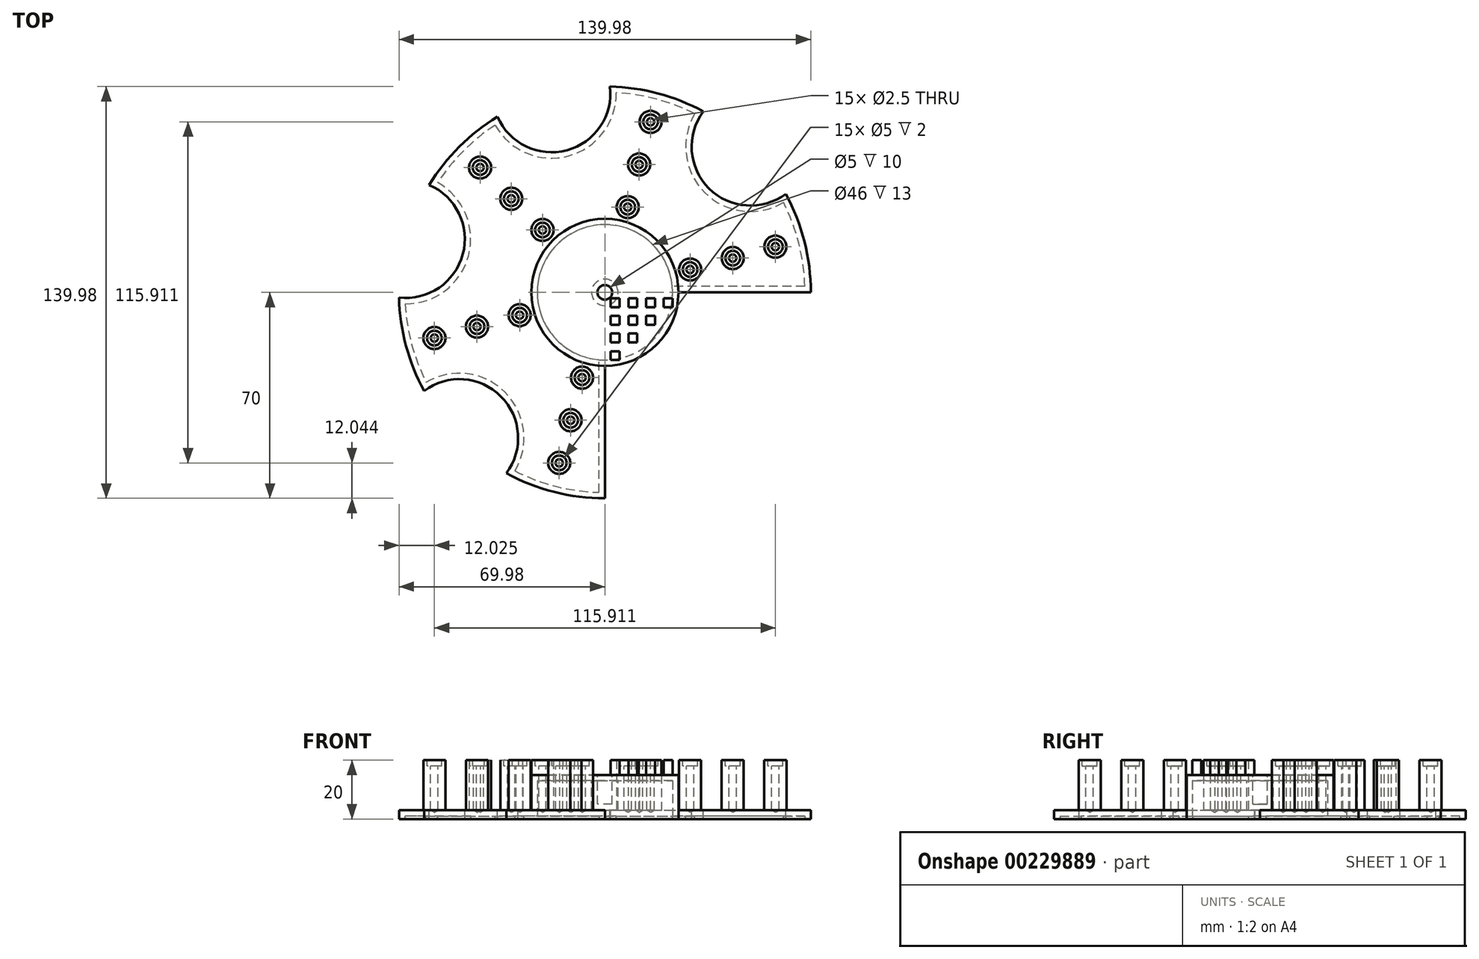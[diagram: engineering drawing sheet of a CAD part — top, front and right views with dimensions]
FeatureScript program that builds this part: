
annotation { "Feature Type Name" : "Feature", "Feature Type Description" : "" }
export const myFeature = defineFeature(function(context is Context, id is Id, definition is map)
    precondition{}
    {
        {
            var Q0;
            Q0=qCreatedBy(makeId("Top.planeOp"),FACE);
            var sketch = newSketch(context, id + "F0", { "sketchPlane" : qUnion([Q0])});
            skCircle(sketch, "E0", {"center": v(0, 0) * mm, "radius": 70 * mm});
            skSolve(sketch);
        }
        {
            var Q0;
            Q0 = qSketchRegion(id + "F0", true);
            extrude(context, id + "F1", {"entities" : qUnion([Q0]), "depth" : 10 * mm, "hasSecondDirection" : true, "secondDirectionOppositeDirection" : true, "secondDirectionDepth" : 5 * mm});
        }
        {
            var Q0;
            Q0=qCreatedBy(makeId("Front.planeOp"),FACE);
            var sketch = newSketch(context, id + "F2", { "sketchPlane" : qUnion([Q0])});
            skLineSegment(sketch, "E1", {"start": v(25, 20) * mm, "end": v(25, -2) * mm});
            skLineSegment(sketch, "E2", {"start": v(25, -2) * mm, "end": v(80, -2) * mm});
            skLineSegment(sketch, "E3", {"start": v(80, -2) * mm, "end": v(80, 20) * mm});
            skLineSegment(sketch, "E4", {"start": v(80, 20) * mm, "end": v(25, 20) * mm});
            skLineSegment(sketch, "E5", {"start": v(0, 50.21) * mm, "end": v(0, -31.63) * mm, "construction": true});
            skSolve(sketch);
        }
        {
            var Q0;
            Q0 = qSketchRegion(id + "F2", true);
            var Q1;
            Q1=sQuery(id+"F2.wireOp",EDGE,"E5");
            revolve(context, id + "F3", {"operationType" : NewBodyOperationType.REMOVE, "entities" : qUnion([Q0]), "axis" : qUnion([Q1]), "revolveType" : RevolveType.FULL, "oppositeDirection" : true});
        }
        {
            var Q0;
            Q0=makeQuery(id+"F1.opExtrude","CAP_FACE",FACE,{"disambiguationData":[OSD([sQuery(id+"F0.wireOp",EDGE,"E0")])],"isStart":false});
            var sketch = newSketch(context, id + "F4", { "sketchPlane" : qUnion([Q0])});
            skCircle(sketch, "E6", {"center": v(0, 0) * mm, "radius": 2.5 * mm});
            skSolve(sketch);
        }
        {
            var Q0;
            Q0 = qSketchRegion(id + "F4", true);
            extrude(context, id + "F5", {"entities" : qUnion([Q0]), "operationType" : NewBodyOperationType.REMOVE, "oppositeDirection" : true, "depth" : 10 * mm});
        }
        {
            var Q0;
            Q0=makeQuery(id+"F3.boolean.opBoolean","COPY",FACE,{"derivedFrom":makeQuery(id+"F3.opRevolve","SWEPT_FACE",FACE,{"disambiguationData":[OSD([sQuery(id+"F2.wireOp",EDGE,"E2")])]})});
            var sketch = newSketch(context, id + "F6", { "sketchPlane" : qUnion([Q0])});
            skLineSegment(sketch, "E7", {"start": v(0, 0) * mm, "end": v(-22.8, 85.11) * mm, "construction": true});
            skLineSegment(sketch, "E8", {"start": v(0, 0) * mm, "end": v(55.72, 55.72) * mm, "construction": true});
            skLineSegment(sketch, "E9", {"start": v(0, 0) * mm, "end": v(-80.55, 21.58) * mm, "construction": true});
            skLineSegment(sketch, "E10", {"start": v(0, 0) * mm, "end": v(-61.33, -61.33) * mm, "construction": true});
            skCircle(sketch, "E11", {"center": v(49.5, 49.5) * mm, "radius": 20 * mm});
            skCircle(sketch, "E12", {"center": v(-18.12, 67.61) * mm, "radius": 20 * mm});
            skCircle(sketch, "E13", {"center": v(-67.61, 18.12) * mm, "radius": 20 * mm});
            skCircle(sketch, "E14", {"center": v(-49.5, -49.5) * mm, "radius": 20 * mm});
            skSolve(sketch);
        }
        {
            var Q0;
            Q0 = qSketchRegion(id + "F6", true);
            extrude(context, id + "F7", {"entities" : qUnion([Q0]), "operationType" : NewBodyOperationType.REMOVE, "endBound" : BoundingType.THROUGH_ALL, "oppositeDirection" : true, "depth" : 25 * mm});
        }
        {
            var Q0;
            Q0=makeQuery(id+"F3.boolean.opBoolean","COPY",FACE,{"derivedFrom":makeQuery(id+"F3.opRevolve","SWEPT_FACE",FACE,{"disambiguationData":[OSD([sQuery(id+"F2.wireOp",EDGE,"E2")])]})});
            var sketch = newSketch(context, id + "F8", { "sketchPlane" : qUnion([Q0])});
            skArc(sketch, "E15", {"start": v(0, -25) * mm, "mid": v(17.68, -17.68) * mm, "end": v(25, 0) * mm});
            skLineSegment(sketch, "E16", {"start": v(80, 0) * mm, "end": v(25, 0) * mm});
            skLineSegment(sketch, "E17", {"start": v(0, -80) * mm, "end": v(0, -25) * mm});
            skArc(sketch, "E18", {"start": v(0, -80) * mm, "mid": v(56.57, -56.57) * mm, "end": v(80, 0) * mm});
            skPoint(sketch, "E19.orphan", {"position": v(88.68, 0) * mm});
            skPoint(sketch, "E20.orphan", {"position": v(0, -96.77) * mm});
            skSolve(sketch);
        }
        {
            var Q0;
            Q0 = qSketchRegion(id + "F8", true);
            extrude(context, id + "F9", {"entities" : qUnion([Q0]), "operationType" : NewBodyOperationType.REMOVE, "oppositeDirection" : true, "depth" : 25 * mm});
        }
        {
            var Q0;
            Q0=makeQuery(id+"F1.opExtrude","CAP_FACE",FACE,{"disambiguationData":[OSD([sQuery(id+"F0.wireOp",EDGE,"E0")])],"isStart":true});
            shell(context, id + "F10", {"entities" : qUnion([Q0]), "thickness" : 2 * mm});
        }
        {
            var Q0;
            Q0=makeQuery(id+"F3.boolean.opBoolean","COPY",FACE,{"derivedFrom":makeQuery(id+"F3.opRevolve","SWEPT_FACE",FACE,{"disambiguationData":[OSD([sQuery(id+"F2.wireOp",EDGE,"E2")])]})});
            var sketch = newSketch(context, id + "F11", { "sketchPlane" : qUnion([Q0])});
            skLineSegment(sketch, "E21", {"start": v(0, 0) * mm, "end": v(122.14, 32.73) * mm, "construction": true});
            skCircle(sketch, "E22", {"center": v(0, 0) * mm, "radius": 30 * mm, "construction": true});
            skCircle(sketch, "E23", {"center": v(0, 0) * mm, "radius": 45 * mm, "construction": true});
            skCircle(sketch, "E24", {"center": v(0, 0) * mm, "radius": 60 * mm, "construction": true});
            skCircle(sketch, "E25", {"center": v(28.98, 7.76) * mm, "radius": 3.75 * mm});
            skCircle(sketch, "E26", {"center": v(43.47, 11.65) * mm, "radius": 3.75 * mm});
            skCircle(sketch, "E27", {"center": v(57.96, 15.53) * mm, "radius": 3.75 * mm});
            skPoint(sketch, "E28.center", {"position": v(-7.8, -0.15) * mm});
            skLineSegment(sketch, "E29", {"start": v(0, 0) * mm, "end": v(23.5, 87.68) * mm, "construction": true});
            skLineSegment(sketch, "E30", {"start": v(0, 0) * mm, "end": v(-59.73, 59.73) * mm, "construction": true});
            skLineSegment(sketch, "E31", {"start": v(0, 0) * mm, "end": v(-84.8, -22.72) * mm, "construction": true});
            skLineSegment(sketch, "E32", {"start": v(0, 0) * mm, "end": v(-19.57, -73.02) * mm, "construction": true});
            skCircle(sketch, "E33.1.0", {"center": v(11.65, 43.47) * mm, "radius": 3.75 * mm});
            skCircle(sketch, "E33.1.1", {"center": v(7.76, 28.98) * mm, "radius": 3.75 * mm});
            skCircle(sketch, "E33.1.2", {"center": v(15.53, 57.96) * mm, "radius": 3.75 * mm});
            skCircle(sketch, "E33.2.0", {"center": v(-31.82, 31.82) * mm, "radius": 3.75 * mm});
            skCircle(sketch, "E33.2.1", {"center": v(-21.21, 21.21) * mm, "radius": 3.75 * mm});
            skCircle(sketch, "E33.2.2", {"center": v(-42.43, 42.43) * mm, "radius": 3.75 * mm});
            skCircle(sketch, "E33.3.0", {"center": v(-43.47, -11.65) * mm, "radius": 3.75 * mm});
            skCircle(sketch, "E33.3.1", {"center": v(-28.98, -7.76) * mm, "radius": 3.75 * mm});
            skCircle(sketch, "E33.3.2", {"center": v(-57.96, -15.53) * mm, "radius": 3.75 * mm});
            skCircle(sketch, "E33.4.0", {"center": v(-11.65, -43.47) * mm, "radius": 3.75 * mm});
            skCircle(sketch, "E33.4.1", {"center": v(-7.76, -28.98) * mm, "radius": 3.75 * mm});
            skCircle(sketch, "E33.4.2", {"center": v(-15.53, -57.96) * mm, "radius": 3.75 * mm});
            skSolve(sketch);
        }
        {
            var Q0;
            Q0 = qSketchRegion(id + "F11", true);
            extrude(context, id + "F12", {"entities" : qUnion([Q0]), "operationType" : NewBodyOperationType.ADD, "depth" : 17 * mm});
        }
        {
            var Q0;
            Q0=makeQuery(id+"F12.opExtrude","CAP_FACE",FACE,{"disambiguationData":[OSD([sQuery(id+"F11.wireOp",EDGE,"E25")])],"isStart":false});
            var sketch = newSketch(context, id + "F13", { "sketchPlane" : qUnion([Q0])});
            skPoint(sketch, "E34", {"position": v(28.98, 7.76) * mm});
            skLineSegment(sketch, "E35", {"start": v(0, 0) * mm, "end": v(74.38, 19.93) * mm, "construction": true});
            skLineSegment(sketch, "E36", {"start": v(0, 0) * mm, "end": v(18.58, 69.33) * mm, "construction": true});
            skLineSegment(sketch, "E37", {"start": v(0, 0) * mm, "end": v(-53.55, 53.55) * mm, "construction": true});
            skLineSegment(sketch, "E38", {"start": v(0, 0) * mm, "end": v(-72.44, -19.4) * mm, "construction": true});
            skLineSegment(sketch, "E39", {"start": v(0, 0) * mm, "end": v(-17, -63.45) * mm, "construction": true});
            skCircle(sketch, "E40", {"center": v(0, 0) * mm, "radius": 30 * mm, "construction": true});
            skCircle(sketch, "E41", {"center": v(0, 0) * mm, "radius": 45 * mm, "construction": true});
            skCircle(sketch, "E42", {"center": v(0, 0) * mm, "radius": 60 * mm, "construction": true});
            skPoint(sketch, "E43", {"position": v(43.47, 11.65) * mm});
            skPoint(sketch, "E44", {"position": v(57.96, 15.53) * mm});
            skPoint(sketch, "E45", {"position": v(15.53, 57.96) * mm});
            skPoint(sketch, "E46", {"position": v(11.65, 43.47) * mm});
            skPoint(sketch, "E47", {"position": v(7.76, 28.98) * mm});
            skPoint(sketch, "E48", {"position": v(-42.43, 42.43) * mm});
            skPoint(sketch, "E49", {"position": v(-31.82, 31.82) * mm});
            skPoint(sketch, "E50", {"position": v(-21.21, 21.21) * mm});
            skPoint(sketch, "E51", {"position": v(-57.96, -15.53) * mm});
            skPoint(sketch, "E52", {"position": v(-43.47, -11.65) * mm});
            skPoint(sketch, "E53", {"position": v(-28.98, -7.76) * mm});
            skPoint(sketch, "E54", {"position": v(-7.76, -28.98) * mm});
            skPoint(sketch, "E55", {"position": v(-11.65, -43.47) * mm});
            skPoint(sketch, "E56", {"position": v(-15.53, -57.96) * mm});
            skSolve(sketch);
        }
        {
            var Q0;
            Q0=sQuery(id+"F13.wireOp",VERTEX,"E34");
            var Q1;
            Q1=sQuery(id+"F13.wireOp",VERTEX,"E43");
            var Q2;
            Q2=sQuery(id+"F13.wireOp",VERTEX,"E44");
            var Q3;
            Q3=sQuery(id+"F13.wireOp",VERTEX,"E47");
            var Q4;
            Q4=sQuery(id+"F13.wireOp",VERTEX,"E46");
            var Q5;
            Q5=sQuery(id+"F13.wireOp",VERTEX,"E45");
            var Q6;
            Q6=sQuery(id+"F13.wireOp",VERTEX,"E50");
            var Q7;
            Q7=sQuery(id+"F13.wireOp",VERTEX,"E49");
            var Q8;
            Q8=sQuery(id+"F13.wireOp",VERTEX,"E48");
            var Q9;
            Q9=sQuery(id+"F13.wireOp",VERTEX,"E53");
            var Q10;
            Q10=sQuery(id+"F13.wireOp",VERTEX,"E52");
            var Q11;
            Q11=sQuery(id+"F13.wireOp",VERTEX,"E51");
            var Q12;
            Q12=sQuery(id+"F13.wireOp",VERTEX,"E54");
            var Q13;
            Q13=sQuery(id+"F13.wireOp",VERTEX,"E55");
            var Q14;
            Q14=sQuery(id+"F13.wireOp",VERTEX,"E56");
            var Q15;
            Q15=makeQuery(id+"F1.opExtrude","SWEPT_BODY",BODY,{"disambiguationData":[OSD([sQuery(id+"F0.wireOp",EDGE,"E0")])]});
            hole(context, id + "F14", {"style" : HoleStyle.C_BORE, "endStyle" : HoleEndStyle.BLIND, "holeDiameter" : 2.5 * mm, "cBoreDiameter" : 5 * mm, "cBoreDepth" : 2 * mm, "holeDepth" : 17 * mm, "startFromSketch" : true, "locations" : qUnion([Q0, Q1, Q2, Q3, Q4, Q5, Q6, Q7, Q8, Q9, Q10, Q11, Q12, Q13, Q14]), "scope" : qUnion([Q15])});
        }
        {
            var Q0;
            Q0=makeQuery(id+"F1.opExtrude","CAP_FACE",FACE,{"disambiguationData":[OSD([sQuery(id+"F0.wireOp",EDGE,"E0")])],"isStart":false});
            var sketch = newSketch(context, id + "F15", { "sketchPlane" : qUnion([Q0])});
            skLineSegment(sketch, "E57.bottom", {"start": v(2, -2) * mm, "end": v(5, -2) * mm});
            skLineSegment(sketch, "E57.top", {"start": v(2, -5) * mm, "end": v(5, -5) * mm});
            skLineSegment(sketch, "E57.left", {"start": v(2, -2) * mm, "end": v(2, -5) * mm});
            skLineSegment(sketch, "E57.right", {"start": v(5, -2) * mm, "end": v(5, -5) * mm});
            skLineSegment(sketch, "E58", {"start": v(3.5, -0.44) * mm, "end": v(3.5, -30.43) * mm, "construction": true});
            skLineSegment(sketch, "E59", {"start": v(1.86, -3.5) * mm, "end": v(29.83, -3.5) * mm, "construction": true});
            skLineSegment(sketch, "E60", {"start": v(9.5, -0.44) * mm, "end": v(9.5, -30.43) * mm, "construction": true});
            skLineSegment(sketch, "E61", {"start": v(15.5, -0.44) * mm, "end": v(15.5, -30.43) * mm, "construction": true});
            skLineSegment(sketch, "E62", {"start": v(21.5, -0.44) * mm, "end": v(21.5, -30.43) * mm, "construction": true});
            skLineSegment(sketch, "E63", {"start": v(29.83, -9.5) * mm, "end": v(1.86, -9.5) * mm, "construction": true});
            skLineSegment(sketch, "E64", {"start": v(29.83, -15.5) * mm, "end": v(1.86, -15.5) * mm, "construction": true});
            skLineSegment(sketch, "E65", {"start": v(29.83, -21.5) * mm, "end": v(1.86, -21.5) * mm, "construction": true});
            skLineSegment(sketch, "E66", {"start": v(27.5, -0.44) * mm, "end": v(27.5, -30.43) * mm, "construction": true});
            skLineSegment(sketch, "E67", {"start": v(1.86, -27.5) * mm, "end": v(29.83, -27.5) * mm, "construction": true});
            skLineSegment(sketch, "E68.0.1.0", {"start": v(2, -8) * mm, "end": v(2, -11) * mm});
            skLineSegment(sketch, "E68.0.1.1", {"start": v(2, -8) * mm, "end": v(5, -8) * mm});
            skLineSegment(sketch, "E68.0.1.2", {"start": v(2, -11) * mm, "end": v(5, -11) * mm});
            skLineSegment(sketch, "E68.0.1.3", {"start": v(5, -8) * mm, "end": v(5, -11) * mm});
            skLineSegment(sketch, "E68.0.2.0", {"start": v(2, -14) * mm, "end": v(2, -17) * mm});
            skLineSegment(sketch, "E68.0.2.1", {"start": v(2, -14) * mm, "end": v(5, -14) * mm});
            skLineSegment(sketch, "E68.0.2.2", {"start": v(2, -17) * mm, "end": v(5, -17) * mm});
            skLineSegment(sketch, "E68.0.2.3", {"start": v(5, -14) * mm, "end": v(5, -17) * mm});
            skLineSegment(sketch, "E68.0.3.0", {"start": v(2, -20) * mm, "end": v(2, -23) * mm});
            skLineSegment(sketch, "E68.0.3.1", {"start": v(2, -20) * mm, "end": v(5, -20) * mm});
            skLineSegment(sketch, "E68.0.3.2", {"start": v(2, -23) * mm, "end": v(5, -23) * mm});
            skLineSegment(sketch, "E68.0.3.3", {"start": v(5, -20) * mm, "end": v(5, -23) * mm});
            skLineSegment(sketch, "E68.1.0.0", {"start": v(8, -2) * mm, "end": v(8, -5) * mm});
            skLineSegment(sketch, "E68.1.0.1", {"start": v(8, -2) * mm, "end": v(11, -2) * mm});
            skLineSegment(sketch, "E68.1.0.2", {"start": v(8, -5) * mm, "end": v(11, -5) * mm});
            skLineSegment(sketch, "E68.1.0.3", {"start": v(11, -2) * mm, "end": v(11, -5) * mm});
            skLineSegment(sketch, "E68.1.1.0", {"start": v(8, -8) * mm, "end": v(8, -11) * mm});
            skLineSegment(sketch, "E68.1.1.1", {"start": v(8, -8) * mm, "end": v(11, -8) * mm});
            skLineSegment(sketch, "E68.1.1.2", {"start": v(8, -11) * mm, "end": v(11, -11) * mm});
            skLineSegment(sketch, "E68.1.1.3", {"start": v(11, -8) * mm, "end": v(11, -11) * mm});
            skLineSegment(sketch, "E68.1.2.0", {"start": v(8, -14) * mm, "end": v(8, -17) * mm});
            skLineSegment(sketch, "E68.1.2.1", {"start": v(8, -14) * mm, "end": v(11, -14) * mm});
            skLineSegment(sketch, "E68.1.2.2", {"start": v(8, -17) * mm, "end": v(11, -17) * mm});
            skLineSegment(sketch, "E68.1.2.3", {"start": v(11, -14) * mm, "end": v(11, -17) * mm});
            skLineSegment(sketch, "E68.2.0.0", {"start": v(14, -2) * mm, "end": v(14, -5) * mm});
            skLineSegment(sketch, "E68.2.0.1", {"start": v(14, -2) * mm, "end": v(17, -2) * mm});
            skLineSegment(sketch, "E68.2.0.2", {"start": v(14, -5) * mm, "end": v(17, -5) * mm});
            skLineSegment(sketch, "E68.2.0.3", {"start": v(17, -2) * mm, "end": v(17, -5) * mm});
            skLineSegment(sketch, "E68.2.1.0", {"start": v(14, -8) * mm, "end": v(14, -11) * mm});
            skLineSegment(sketch, "E68.2.1.1", {"start": v(14, -8) * mm, "end": v(17, -8) * mm});
            skLineSegment(sketch, "E68.2.1.2", {"start": v(14, -11) * mm, "end": v(17, -11) * mm});
            skLineSegment(sketch, "E68.2.1.3", {"start": v(17, -8) * mm, "end": v(17, -11) * mm});
            skLineSegment(sketch, "E68.3.0.0", {"start": v(20, -2) * mm, "end": v(20, -5) * mm});
            skLineSegment(sketch, "E68.3.0.1", {"start": v(20, -2) * mm, "end": v(23, -2) * mm});
            skLineSegment(sketch, "E68.3.0.2", {"start": v(20, -5) * mm, "end": v(23, -5) * mm});
            skLineSegment(sketch, "E68.3.0.3", {"start": v(23, -2) * mm, "end": v(23, -5) * mm});
            skLineSegment(sketch, "E68.direction1", {"start": v(2, -5) * mm, "end": v(8, -5) * mm, "construction": true});
            skLineSegment(sketch, "E68.direction2", {"start": v(2, -5) * mm, "end": v(2, -11) * mm, "construction": true});
            skSolve(sketch);
        }
        {
            var Q0;
            Q0 = qSketchRegion(id + "F15", true);
            extrude(context, id + "F16", {"entities" : qUnion([Q0]), "operationType" : NewBodyOperationType.ADD, "depth" : 5 * mm});
        }
    });
